# Revit family: ASH_ArmitageShanks_WallHungWashBasins_Contour21-Accessible-55cm
name_source: partatom
category: Plumbing Fixtures
revit_build: Autodesk Revit MEP 2012 (Build: 20110309_2315(x64)
units: mm (PartAtom-declared; Revit-internal decimal feet)

## types (3) — shared parameters
Accessories = www.idealspec.co.uk
AreaUnits = millimeters
Assembly Code = C1030200
AssetType = Fixed
BasinMaterial = ASH_ArmitageShanks _Sanitaryware_White4_Render
Brand = Armitage Shanks
Category = SanitaryTerminal_WASHHANDBASIN_UK
Color = White
ConnectionType = Plumbing
Default Elevation = 730 mm  [stored 2.39501 ft]
DrainSize = 32 mm  [stored 0.104987 ft]
DurationUnit = year
ECA = Yes
ExpectedLife = 30
Finish = White
IfcExportAs = IfcSanitaryTerminalType
IfcExportType = WASHHANDBASIN
InstallationInstructions = www.idealspec.co.uk/resources.html
LinearUnits = millimeters
ManufacturerURL = www.idealspec.co.uk
Material = Vitreous china
NBSDescription = Wall hung wash basins
NBSReference = 45-35-70/369
NettWeight = 16.9 Kg
NominalDepth = 548 mm
NominalHeight = 195 mm
NominalLength = 548 mm
NominalWidth = 540 mm
Shape = Square
Size = 550 x 550 x 200 mm
Space = Internal
SpareParts = www.fastpart-spares.co.uk
URL = www.idealspec.co.uk
Uniclass2 = Pr_40_20_96_96
Version = 1
VolumeUnits = Litres
WRAS = Yes
WarrantyDescription = Manufacturers warranty
WarrantyDurationParts = 99
WarrantyDurationUnit = year
WashHandBasinMounting = Wall hung
WashHandBasinType = HANDRINSE
WaterEfficientProduct = Yes
zero-valued in all types: CWFU, HWFU, WFU

## per-type parameters (varying)
| type | 1TH | 2TH | BIMObjectName | Description | Features | Model | ModelNumber | ModelReference | Name | ProductInformation |
| S216401 - Contour 21 Accessible Washbasin 55cm No Taphole, No Chainstay Hole, With Overflow | No | No | ASH_ArmitageShanks_WallHungHandRinseBasins_Contour21_S2164 | Contour 21 accessible washbasin 55 cm no taphole, no chainstay hole, with overflow | 55 cm no taphole, no chainstay hole, with overflow | S216401 | S216401 | Contour 21 accessible washbasin 55 cm no taphole, no chainstay hole, with overflow | WallHungHandRinseBasins_Contour21_S2164_ArmitageShanks | www.idealspec.co.uk/assets/datasheet/S216401 |
| S216501 - Contour 21 Accessible Washbasin 55cm 1 Centre Overflow No Chainstay Hole | Yes | No | ASH_ArmitageShanks_WallHungHandRinseBasins_Contour21_S2165 | Contour 21 accessible washbasin 55 cm 1 centre overflow no chainstay hole | 55 cm 1 centre overflow no chainstay hole | S216501 | S216501 | Contour 21 accessible washbasin 55 cm 1 centre overflow no chainstay hole | WallHungHandRinseBasins_Contour21_S2165_ArmitageShanks | www.idealspec.co.uk/assets/datasheet/S216501 |
| S216601 - Contour 21 Accessible Washbasin 55cm 2 Taphole Overflow & Chainstay Hole | No | Yes | ASH_ArmitageShanks_WallHungHandRinseBasins_Contour21_S2166 | Contour 21 accessible washbasin 55 cm 2 taphole overflow & chainstay hole | 55 cm 2 taphole overflow & chainstay hole | S216601 | S216601 | Contour 21 accessible washbasin 55 cm 2 taphole overflow & chainstay hole | WallHungHandRinseBasins_Contour21_S2166_ArmitageShanks | www.idealspec.co.uk/assets/datasheet/S216601 |

note: [stored X ft] marks values corroborated as IEEE doubles in the binary element streams (Revit-internal decimal feet)

## geometry (parser evidence)
native form markers: Blend x5, Sweep x8
no freeform markers — native parametric forms only
